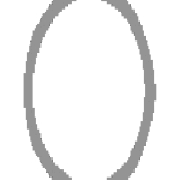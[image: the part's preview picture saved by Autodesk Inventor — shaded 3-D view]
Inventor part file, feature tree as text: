
AUTODESK INVENTOR PART (.ipt)
format: ipt  version: 2021 (Build 250183000, 183)  size: 112,128 bytes
history: native  units: in
note: dims shown in document units (in); Inventor stores cm internally (conversion verified against a paired STEP export)
features: other x4, sketch x3, plane x1
ambient origin geometry x8: Origin, YZ Plane, XZ Plane, XY Plane, X Axis, Y Axis, Z Axis, Center Point
bodies: Solid1 (feature_tree), Body (feature_tree)
feature tree (8):
  other  "Driven Length"
  other  "Frame Generator"
  other  "Start Plane"
  other  "End Plane"
  sketch  "Sketch"  dims[d2=4.559in d4=-0.0in d5=4.559in d6=0.12in d7=0.0in d8=90.0deg d9=4.559in]
  sketch  "Sketch2"  dims[d0=1.0in]
  plane  "Work Plane3"
  sketch  "Sketch3"  dims[d1=0.065in]
